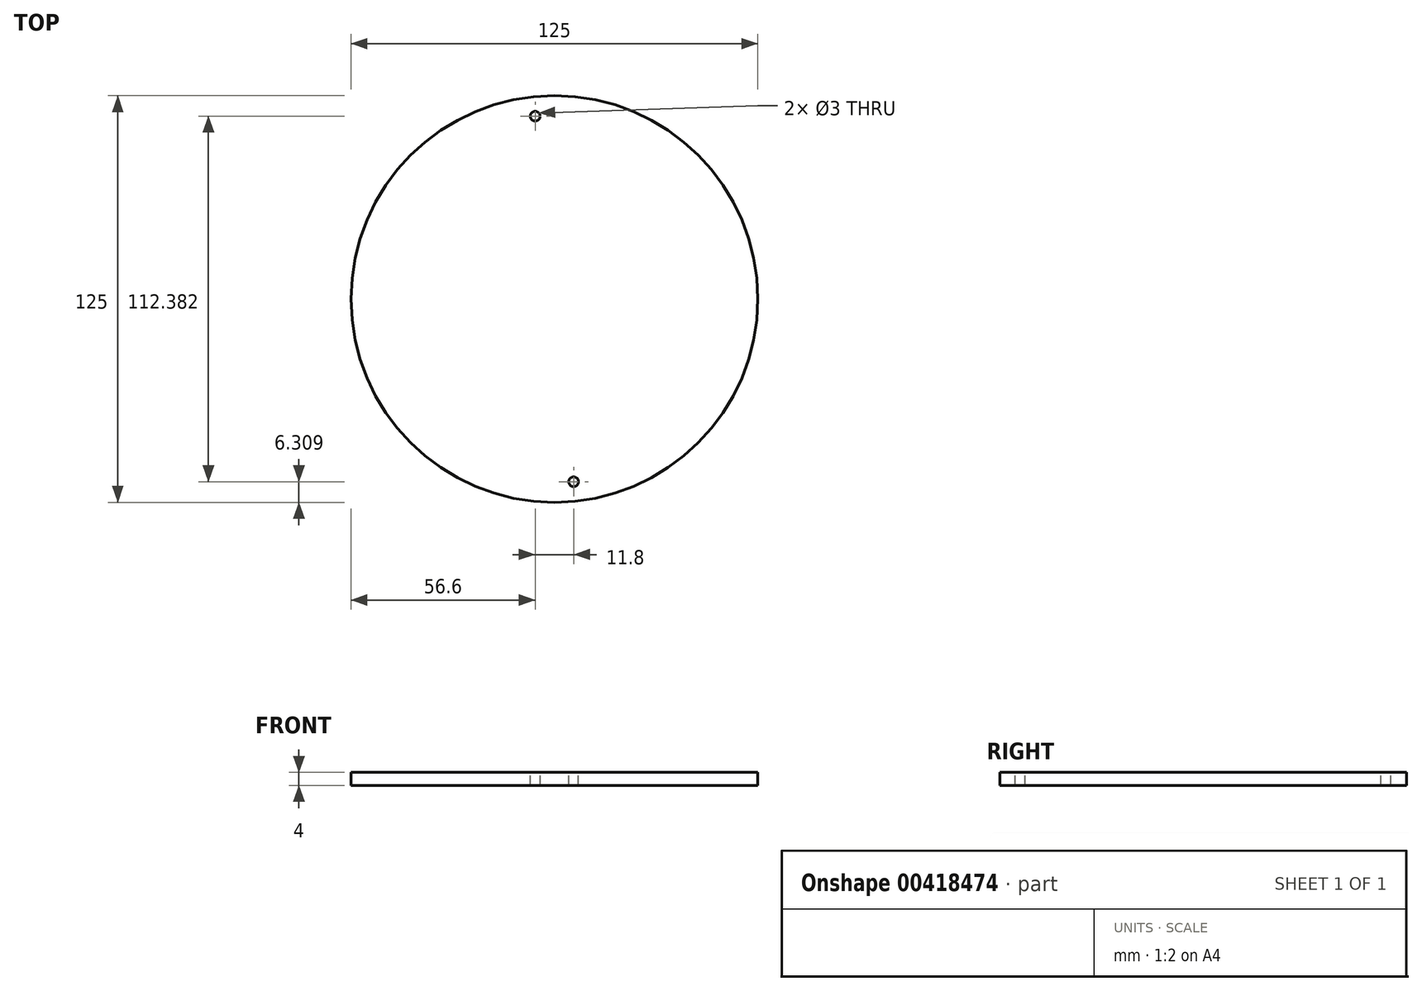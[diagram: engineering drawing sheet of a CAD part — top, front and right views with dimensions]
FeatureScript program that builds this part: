
annotation { "Feature Type Name" : "Feature", "Feature Type Description" : "" }
export const myFeature = defineFeature(function(context is Context, id is Id, definition is map)
    precondition{}
    {
        {
            var Q0;
            Q0=qCreatedBy(makeId("Top.planeOp"),FACE);
            var sketch = newSketch(context, id + "F0", { "sketchPlane" : qUnion([Q0])});
            skCircle(sketch, "E0", {"center": v(0, 0) * mm, "radius": 62.5 * mm});
            skSolve(sketch);
        }
        {
            var Q0;
            Q0 = qSketchRegion(id + "F0", true);
            extrude(context, id + "F1", {"entities" : qUnion([Q0]), "depth" : 4 * mm});
        }
        {
            var Q0;
            Q0=makeQuery(id+"F1.opExtrude","CAP_FACE",FACE,{"disambiguationData":[OSD([sQuery(id+"F0.wireOp",EDGE,"E0")])],"isStart":false});
            var sketch = newSketch(context, id + "F2", { "sketchPlane" : qUnion([Q0])});
            skCircle(sketch, "E1", {"center": v(-5.9, 56.2) * mm, "radius": 1.5 * mm});
            skSolve(sketch);
        }
        {
            var Q0;
            Q0 = qSketchRegion(id + "F2", true);
            extrude(context, id + "F3", {"entities" : qUnion([Q0]), "operationType" : NewBodyOperationType.REMOVE, "endBound" : BoundingType.THROUGH_ALL, "oppositeDirection" : true, "depth" : 25 * mm});
        }
        {
            var Q0;
            Q0=makeQuery(id+"F1.opExtrude","CAP_FACE",FACE,{"disambiguationData":[OSD([sQuery(id+"F0.wireOp",EDGE,"E0")])],"isStart":false});
            var sketch = newSketch(context, id + "F4", { "sketchPlane" : qUnion([Q0])});
            skCircle(sketch, "E2", {"center": v(5.9, -56.2) * mm, "radius": 1.5 * mm});
            skSolve(sketch);
        }
        {
            var Q0;
            Q0=makeQuery(id+"F4.imprint","IMPRINT",FACE,{"disambiguationData":[TD([[makeQuery(id+"F4.imprint","IMPRINT",EDGE,{"derivedFrom":sQuery(id+"F4.wireOp",EDGE,"E2")}),1.0]])]});
            extrude(context, id + "F5", {"entities" : qUnion([Q0]), "operationType" : NewBodyOperationType.REMOVE, "endBound" : BoundingType.THROUGH_ALL, "oppositeDirection" : true, "depth" : 25 * mm});
        }
    });
